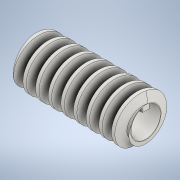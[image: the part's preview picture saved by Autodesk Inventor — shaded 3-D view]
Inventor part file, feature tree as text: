
AUTODESK INVENTOR PART (.ipt)
format: ipt  version: 2021.1 (Build 251245010, 245A)  size: 458,240 bytes
history: native  units: mm (DEFAULTED — no unit token found)
features: other x6, extrude x2, chamfer x2, pattern_circular x2, sketch x2
ambient origin geometry x6: Origin, XZ Plane, X Axis, Y Axis, Z Axis, Center Point
bodies: Solid1 (feature_tree)
feature tree (14):
  extrude  "Base Body"  Depth=16.493545mm
  chamfer  "Chamfer1"  [1 undecoded]
  chamfer  "Chamfer2"  Distance=1.100579mm
  other  "Tooth Sketch"
  other  "Left Tooth"
  pattern_circular  "Left Tooth Pattern"  [2 undecoded]
  other  "Tooth"
  pattern_circular  "Tooth Pattern"  [2 undecoded]
  extrude  "Extrusion2"  Depth=2.38125mm
  other  "Base Body Sketch"
  sketch  "Sketch5"  dims[d4=40.0mm d5=16.493545mm]
  other  "Srf1"
  sketch  "Sketch6"  dims[d6=38.1mm d7=0.0mm d8=1.100579mm d9=3.023817mm d10=1.100579mm d11=3.023817mm d12=19.198622mm d14=3.1425mm d24=19.198622mm d25=23.749mm d26=1.0795mm d27=5.222956mm d28=6.87231mm d29=8.32924mm d30=4.318mm d31=10.0mm d32=110.0mm d33=0.0mm d34=90.0deg d35=90.0deg d36=0.0mm d37=0.0mm d43=10.0mm d45=360.0deg d46=45.0deg d47=45.0deg d49=0.0mm d53=0.0mm d54=48.106173mm d55=0.0mm d56=0.0mm d57=13.744621mm d58=25.4mm d59=0.0mm d60=4.318mm d61=25.4mm d62=110.0mm d63=0.0mm d64=90.0deg d65=90.0deg d66=0.0mm d67=0.0mm d68=10.0mm d69=10.0mm d70=360.0deg d72=10.0mm d74=10.0mm d75=10.0mm d76=0.0mm d77=48.106173mm d78=10.033mm d79=0.0mm d80=0.0mm d85=2.38125mm d86=1.444625mm]
  other  "Pitch Diameter"
note: 5 required parameter values undecoded (feature->parameter linkage not recoverable at this tier; creation-order binding heuristic only, values carry confidence <= 0.55)
